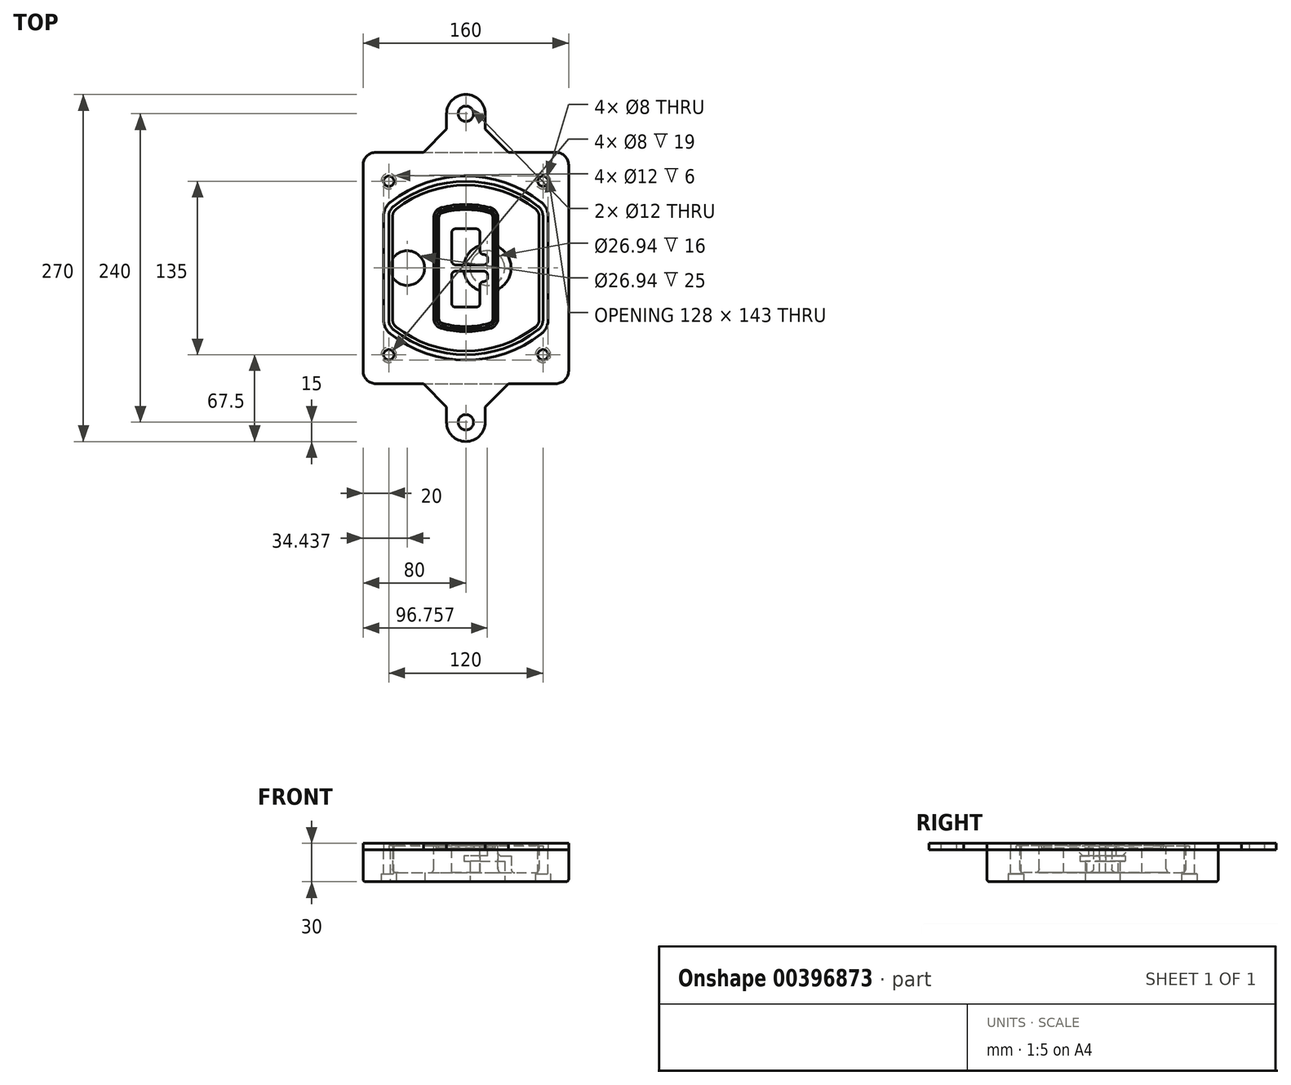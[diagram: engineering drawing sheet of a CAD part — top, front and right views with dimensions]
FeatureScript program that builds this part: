
annotation { "Feature Type Name" : "Feature", "Feature Type Description" : "" }
export const myFeature = defineFeature(function(context is Context, id is Id, definition is map)
    precondition{}
    {
        {
            var Q0;
            Q0=qCreatedBy(makeId("Top.planeOp"),FACE);
            var sketch = newSketch(context, id + "F0", { "sketchPlane" : qUnion([Q0])});
            skPoint(sketch, "E0.rect.middle", {"position": v(0, 0) * mm});
            skLineSegment(sketch, "E1.bottom", {"start": v(-70, -90) * mm, "end": v(70, -90) * mm});
            skLineSegment(sketch, "E1.top", {"start": v(-70, 90) * mm, "end": v(70, 90) * mm});
            skLineSegment(sketch, "E1.left", {"start": v(-80, -80) * mm, "end": v(-80, 80) * mm});
            skLineSegment(sketch, "E1.right", {"start": v(80, -80) * mm, "end": v(80, 80) * mm});
            skLineSegment(sketch, "E2", {"start": v(-80, 90) * mm, "end": v(80, -90) * mm, "construction": true});
            skLineSegment(sketch, "E3", {"start": v(80, 90) * mm, "end": v(-80, -90) * mm, "construction": true});
            skCircle(sketch, "E4", {"center": v(-60, 67.5) * mm, "radius": 4 * mm});
            skCircle(sketch, "E5", {"center": v(60, 67.5) * mm, "radius": 4 * mm});
            skCircle(sketch, "E6", {"center": v(60, -67.5) * mm, "radius": 4 * mm});
            skCircle(sketch, "E7", {"center": v(-60, -67.5) * mm, "radius": 4 * mm});
            skLineSegment(sketch, "E8", {"start": v(-60, 67.5) * mm, "end": v(60, 67.5) * mm, "construction": true});
            skLineSegment(sketch, "E9", {"start": v(60, 67.5) * mm, "end": v(60, -67.5) * mm, "construction": true});
            skLineSegment(sketch, "E10", {"start": v(60, -67.5) * mm, "end": v(-60, -67.5) * mm, "construction": true});
            skLineSegment(sketch, "E11", {"start": v(-60, -67.5) * mm, "end": v(-60, 67.5) * mm, "construction": true});
            skLineSegment(sketch, "E12", {"start": v(-60, 40.3) * mm, "end": v(-60, -40.3) * mm});
            skLineSegment(sketch, "E13", {"start": v(60, 40.3) * mm, "end": v(60, -40.3) * mm});
            skArc(sketch, "E14", {"start": v(56.15, 48.18) * mm, "mid": v(0, 67.5) * mm, "end": v(-56.15, 48.18) * mm});
            skArc(sketch, "E15", {"start": v(-56.15, -48.18) * mm, "mid": v(0, -67.5) * mm, "end": v(56.15, -48.18) * mm});
            skLineSegment(sketch, "E16", {"start": v(-60, 0) * mm, "end": v(60, 0) * mm, "construction": true});
            skPoint(sketch, "E17.visualSharp", {"position": v(-60, -45) * mm});
            skArc(sketch, "E17.filletArc", {"start": v(-60, -40.3) * mm, "mid": v(-58.99, -44.68) * mm, "end": v(-56.15, -48.18) * mm});
            skPoint(sketch, "E18.visualSharp", {"position": v(-60, 45) * mm});
            skArc(sketch, "E18.filletArc", {"start": v(-56.15, 48.18) * mm, "mid": v(-58.99, 44.68) * mm, "end": v(-60, 40.3) * mm});
            skPoint(sketch, "E19.visualSharp", {"position": v(60, 45) * mm});
            skArc(sketch, "E19.filletArc", {"start": v(60, 40.3) * mm, "mid": v(58.99, 44.68) * mm, "end": v(56.15, 48.18) * mm});
            skPoint(sketch, "E20.visualSharp", {"position": v(60, -45) * mm});
            skArc(sketch, "E20.filletArc", {"start": v(56.15, -48.18) * mm, "mid": v(58.99, -44.68) * mm, "end": v(60, -40.3) * mm});
            skPoint(sketch, "E21.visualSharp", {"position": v(-80, 90) * mm});
            skArc(sketch, "E21.filletArc", {"start": v(-70, 90) * mm, "mid": v(-77.07, 87.07) * mm, "end": v(-80, 80) * mm});
            skPoint(sketch, "E22.visualSharp", {"position": v(80, 90) * mm});
            skArc(sketch, "E22.filletArc", {"start": v(80, 80) * mm, "mid": v(77.07, 87.07) * mm, "end": v(70, 90) * mm});
            skPoint(sketch, "E23.visualSharp", {"position": v(80, -90) * mm});
            skArc(sketch, "E23.filletArc", {"start": v(70, -90) * mm, "mid": v(77.07, -87.07) * mm, "end": v(80, -80) * mm});
            skPoint(sketch, "E24.visualSharp", {"position": v(-80, -90) * mm});
            skArc(sketch, "E24.filletArc", {"start": v(-80, -80) * mm, "mid": v(-77.07, -87.07) * mm, "end": v(-70, -90) * mm});
            skArc(sketch, "E25.0", {"start": v(57, 40.3) * mm, "mid": v(56.3, 43.36) * mm, "end": v(54.3, 45.81) * mm});
            skLineSegment(sketch, "E25.1", {"start": v(57, 40.3) * mm, "end": v(57, -40.3) * mm});
            skArc(sketch, "E25.2", {"start": v(54.3, -45.81) * mm, "mid": v(56.3, -43.36) * mm, "end": v(57, -40.3) * mm});
            skArc(sketch, "E25.3", {"start": v(-54.3, -45.81) * mm, "mid": v(0, -64.5) * mm, "end": v(54.3, -45.81) * mm});
            skArc(sketch, "E25.4", {"start": v(-57, -40.3) * mm, "mid": v(-56.3, -43.36) * mm, "end": v(-54.3, -45.81) * mm});
            skArc(sketch, "E25.5", {"start": v(54.3, 45.81) * mm, "mid": v(0, 64.5) * mm, "end": v(-54.3, 45.81) * mm});
            skLineSegment(sketch, "E25.6", {"start": v(-57, 40.3) * mm, "end": v(-57, -40.3) * mm});
            skArc(sketch, "E25.7", {"start": v(-54.3, 45.81) * mm, "mid": v(-56.3, 43.36) * mm, "end": v(-57, 40.3) * mm});
            skArc(sketch, "E26.0", {"start": v(-58.62, 51.33) * mm, "mid": v(-62.58, 46.43) * mm, "end": v(-64, 40.3) * mm});
            skArc(sketch, "E26.1", {"start": v(58.62, 51.33) * mm, "mid": v(0, 71.5) * mm, "end": v(-58.62, 51.33) * mm});
            skArc(sketch, "E26.2", {"start": v(64, 40.3) * mm, "mid": v(62.58, 46.43) * mm, "end": v(58.62, 51.33) * mm});
            skLineSegment(sketch, "E26.3", {"start": v(64, 40.3) * mm, "end": v(64, -40.3) * mm});
            skArc(sketch, "E26.4", {"start": v(58.62, -51.33) * mm, "mid": v(62.58, -46.43) * mm, "end": v(64, -40.3) * mm});
            skLineSegment(sketch, "E26.5", {"start": v(-64, 40.3) * mm, "end": v(-64, -40.3) * mm});
            skArc(sketch, "E26.6", {"start": v(-58.62, -51.33) * mm, "mid": v(0, -71.5) * mm, "end": v(58.62, -51.33) * mm});
            skArc(sketch, "E26.7", {"start": v(-64, -40.3) * mm, "mid": v(-62.58, -46.43) * mm, "end": v(-58.62, -51.33) * mm});
            skLineSegment(sketch, "E27", {"start": v(-33, 90) * mm, "end": v(-15, 108) * mm});
            skLineSegment(sketch, "E28", {"start": v(33, 90) * mm, "end": v(15, 108) * mm});
            skLineSegment(sketch, "E29", {"start": v(15, 108) * mm, "end": v(15, 120) * mm});
            skLineSegment(sketch, "E30", {"start": v(-15, 108) * mm, "end": v(-15, 120) * mm});
            skArc(sketch, "E31", {"start": v(15, 120) * mm, "mid": v(0, 135) * mm, "end": v(-15, 120) * mm});
            skCircle(sketch, "E32", {"center": v(0, 120) * mm, "radius": 6 * mm});
            skLineSegment(sketch, "E33.MirrorCS", {"start": v(15, -108) * mm, "end": v(15, -120) * mm});
            skArc(sketch, "E34.MirrorCS", {"start": v(15, -120) * mm, "mid": v(0, -135) * mm, "end": v(-15, -120) * mm});
            skCircle(sketch, "E35.MirrorC", {"center": v(0, -120) * mm, "radius": 6 * mm});
            skLineSegment(sketch, "E36.MirrorCS", {"start": v(-15, -108) * mm, "end": v(-15, -120) * mm});
            skLineSegment(sketch, "E37.MirrorCS", {"start": v(33, -90) * mm, "end": v(15, -108) * mm});
            skLineSegment(sketch, "E38.MirrorCS", {"start": v(-33, -90) * mm, "end": v(-15, -108) * mm});
            skSolve(sketch);
        }
        {
            var Q0;
            Q0=makeQuery(id+"F0.imprint","IMPRINT",FACE,{"disambiguationData":[TD([[makeQuery(id+"F0.imprint","IMPRINT",EDGE,{"derivedFrom":sQuery(id+"F0.wireOp",EDGE,"E1.bottom")}),1.0]])]});
            var Q1;
            Q1=makeQuery(id+"F0.imprint","IMPRINT",FACE,{"disambiguationData":[TD([[makeQuery(id+"F0.imprint","IMPRINT",EDGE,{"derivedFrom":sQuery(id+"F0.wireOp",EDGE,"E12")}),1.0]])]});
            var Q2;
            Q2=makeQuery(id+"F0.imprint","IMPRINT",FACE,{"disambiguationData":[TD([[makeQuery(id+"F0.imprint","IMPRINT",EDGE,{"derivedFrom":sQuery(id+"F0.wireOp",EDGE,"E25.0")}),1.0]])]});
            var Q3;
            Q3=makeQuery(id+"F0.imprint","IMPRINT",FACE,{"disambiguationData":[TD([[makeQuery(id+"F0.imprint","IMPRINT",EDGE,{"derivedFrom":sQuery(id+"F0.wireOp",EDGE,"E12")}),-1.0]])]});
            extrude(context, id + "F1", {"entities" : qUnion([Q0, Q1, Q2, Q3]), "oppositeDirection" : true, "depth" : 25 * mm});
        }
        {
            var Q0;
            Q0=makeQuery(id+"F0.imprint","IMPRINT",FACE,{"disambiguationData":[TD([[makeQuery(id+"F0.imprint","IMPRINT",EDGE,{"derivedFrom":sQuery(id+"F0.wireOp",EDGE,"E12")}),1.0]])]});
            extrude(context, id + "F2", {"entities" : qUnion([Q0]), "operationType" : NewBodyOperationType.ADD, "depth" : 3 * mm});
        }
        {
            var Q0;
            Q0=makeQuery(id+"F0.imprint","IMPRINT",FACE,{"disambiguationData":[TD([[makeQuery(id+"F0.imprint","IMPRINT",EDGE,{"derivedFrom":sQuery(id+"F0.wireOp",EDGE,"E25.0")}),1.0]])]});
            extrude(context, id + "F3", {"entities" : qUnion([Q0]), "operationType" : NewBodyOperationType.REMOVE, "oppositeDirection" : true, "depth" : 18 * mm});
        }
        {
            var Q0;
            Q0=makeQuery(id+"F2.opExtrude","CAP_FACE",FACE,{"disambiguationData":[OSD([sQuery(id+"F0.wireOp",EDGE,"E12"),sQuery(id+"F0.wireOp",EDGE,"E13"),sQuery(id+"F0.wireOp",EDGE,"E14"),sQuery(id+"F0.wireOp",EDGE,"E15"),sQuery(id+"F0.wireOp",EDGE,"E17.filletArc"),sQuery(id+"F0.wireOp",EDGE,"E18.filletArc"),sQuery(id+"F0.wireOp",EDGE,"E19.filletArc"),sQuery(id+"F0.wireOp",EDGE,"E20.filletArc"),sQuery(id+"F0.wireOp",EDGE,"E25.0"),sQuery(id+"F0.wireOp",EDGE,"E25.1"),sQuery(id+"F0.wireOp",EDGE,"E25.2"),sQuery(id+"F0.wireOp",EDGE,"E25.3"),sQuery(id+"F0.wireOp",EDGE,"E25.4"),sQuery(id+"F0.wireOp",EDGE,"E25.5"),sQuery(id+"F0.wireOp",EDGE,"E25.6"),sQuery(id+"F0.wireOp",EDGE,"E25.7")])],"isStart":false});
            var sketch = newSketch(context, id + "F4", { "sketchPlane" : qUnion([Q0])});
            skArc(sketch, "E39.0", {"start": v(-19.08, -46.97) * mm, "mid": v(0, -49.5) * mm, "end": v(19.08, -46.97) * mm});
            skArc(sketch, "E40.0", {"start": v(19.08, 46.97) * mm, "mid": v(0, 49.5) * mm, "end": v(-19.08, 46.97) * mm});
            skLineSegment(sketch, "E41", {"start": v(-25, 39.25) * mm, "end": v(-25, -39.25) * mm});
            skLineSegment(sketch, "E42", {"start": v(25, 39.25) * mm, "end": v(25, -39.25) * mm});
            skLineSegment(sketch, "E43", {"start": v(-25, 45.1) * mm, "end": v(25, 45.1) * mm, "construction": true});
            skLineSegment(sketch, "E44", {"start": v(-25, -45.1) * mm, "end": v(25, -45.1) * mm, "construction": true});
            skPoint(sketch, "E45.visualSharp", {"position": v(-25, 45.1) * mm});
            skArc(sketch, "E45.filletArc", {"start": v(-19.08, 46.97) * mm, "mid": v(-23.35, 44.11) * mm, "end": v(-25, 39.25) * mm});
            skPoint(sketch, "E46.visualSharp", {"position": v(25, 45.1) * mm});
            skArc(sketch, "E46.filletArc", {"start": v(25, 39.25) * mm, "mid": v(23.35, 44.11) * mm, "end": v(19.08, 46.97) * mm});
            skPoint(sketch, "E47.visualSharp", {"position": v(25, -45.1) * mm});
            skArc(sketch, "E47.filletArc", {"start": v(19.08, -46.97) * mm, "mid": v(23.35, -44.11) * mm, "end": v(25, -39.25) * mm});
            skPoint(sketch, "E48.visualSharp", {"position": v(-25, -45.1) * mm});
            skArc(sketch, "E48.filletArc", {"start": v(-25, -39.25) * mm, "mid": v(-23.35, -44.11) * mm, "end": v(-19.08, -46.97) * mm});
            skArc(sketch, "E49.0", {"start": v(54.3, 45.81) * mm, "mid": v(0, 64.5) * mm, "end": v(-54.3, 45.81) * mm});
            skArc(sketch, "E49.1", {"start": v(-54.3, 45.81) * mm, "mid": v(-56.3, 43.36) * mm, "end": v(-57, 40.3) * mm});
            skLineSegment(sketch, "E49.2", {"start": v(-57, 40.3) * mm, "end": v(-57, -40.3) * mm});
            skArc(sketch, "E49.3", {"start": v(-57, -40.3) * mm, "mid": v(-56.3, -43.36) * mm, "end": v(-54.3, -45.81) * mm});
            skArc(sketch, "E49.4", {"start": v(-54.3, -45.81) * mm, "mid": v(0, -64.5) * mm, "end": v(54.3, -45.81) * mm});
            skArc(sketch, "E49.5", {"start": v(54.3, -45.81) * mm, "mid": v(56.3, -43.36) * mm, "end": v(57, -40.3) * mm});
            skLineSegment(sketch, "E49.6", {"start": v(57, 40.3) * mm, "end": v(57, -40.3) * mm});
            skArc(sketch, "E49.7", {"start": v(57, 40.3) * mm, "mid": v(56.3, 43.36) * mm, "end": v(54.3, 45.81) * mm});
            skLineSegment(sketch, "E50.0", {"start": v(23, 39.25) * mm, "end": v(23, -39.25) * mm});
            skArc(sketch, "E50.1", {"start": v(18.56, -45.04) * mm, "mid": v(21.76, -42.9) * mm, "end": v(23, -39.25) * mm});
            skArc(sketch, "E50.2", {"start": v(-18.56, -45.04) * mm, "mid": v(0, -47.5) * mm, "end": v(18.56, -45.04) * mm});
            skArc(sketch, "E50.3", {"start": v(-23, -39.25) * mm, "mid": v(-21.76, -42.9) * mm, "end": v(-18.56, -45.04) * mm});
            skLineSegment(sketch, "E50.4", {"start": v(-23, 39.25) * mm, "end": v(-23, -39.25) * mm});
            skArc(sketch, "E50.5", {"start": v(23, 39.25) * mm, "mid": v(21.76, 42.9) * mm, "end": v(18.56, 45.04) * mm});
            skArc(sketch, "E50.6", {"start": v(-18.56, 45.04) * mm, "mid": v(-21.76, 42.9) * mm, "end": v(-23, 39.25) * mm});
            skArc(sketch, "E50.7", {"start": v(18.56, 45.04) * mm, "mid": v(0, 47.5) * mm, "end": v(-18.56, 45.04) * mm});
            skArc(sketch, "E51.0", {"start": v(21, 39.25) * mm, "mid": v(20.18, 41.68) * mm, "end": v(18.04, 43.1) * mm});
            skLineSegment(sketch, "E51.1", {"start": v(21, 39.25) * mm, "end": v(21, -39.25) * mm});
            skArc(sketch, "E51.2", {"start": v(18.04, -43.1) * mm, "mid": v(20.18, -41.68) * mm, "end": v(21, -39.25) * mm});
            skArc(sketch, "E51.3", {"start": v(-18.04, -43.1) * mm, "mid": v(0, -45.5) * mm, "end": v(18.04, -43.1) * mm});
            skArc(sketch, "E51.4", {"start": v(-21, -39.25) * mm, "mid": v(-20.18, -41.68) * mm, "end": v(-18.04, -43.1) * mm});
            skArc(sketch, "E51.5", {"start": v(18.04, 43.1) * mm, "mid": v(0, 45.5) * mm, "end": v(-18.04, 43.1) * mm});
            skLineSegment(sketch, "E51.6", {"start": v(-21, 39.25) * mm, "end": v(-21, -39.25) * mm});
            skArc(sketch, "E51.7", {"start": v(-18.04, 43.1) * mm, "mid": v(-20.18, 41.68) * mm, "end": v(-21, 39.25) * mm});
            skLineSegment(sketch, "E52", {"start": v(-25, 0) * mm, "end": v(25, 0) * mm, "construction": true});
            skLineSegment(sketch, "E53", {"start": v(-11, 5.5) * mm, "end": v(-11, 27.5) * mm});
            skLineSegment(sketch, "E54", {"start": v(-8, 30.5) * mm, "end": v(8, 30.5) * mm});
            skLineSegment(sketch, "E55", {"start": v(11, 27.5) * mm, "end": v(11, 13.5) * mm});
            skLineSegment(sketch, "E56", {"start": v(14, 10.5) * mm, "end": v(14, 10.5) * mm});
            skLineSegment(sketch, "E57", {"start": v(17, 7.5) * mm, "end": v(17, 5.5) * mm});
            skLineSegment(sketch, "E58", {"start": v(14, 2.5) * mm, "end": v(-8, 2.5) * mm});
            skPoint(sketch, "E59.visualSharp", {"position": v(-11, 30.5) * mm});
            skArc(sketch, "E59.filletArc", {"start": v(-8, 30.5) * mm, "mid": v(-10.12, 29.62) * mm, "end": v(-11, 27.5) * mm});
            skPoint(sketch, "E60.visualSharp", {"position": v(11, 30.5) * mm});
            skArc(sketch, "E60.filletArc", {"start": v(11, 27.5) * mm, "mid": v(10.12, 29.62) * mm, "end": v(8, 30.5) * mm});
            skPoint(sketch, "E61.visualSharp", {"position": v(11, 10.5) * mm});
            skArc(sketch, "E61.filletArc", {"start": v(11, 13.5) * mm, "mid": v(11.88, 11.38) * mm, "end": v(14, 10.5) * mm});
            skPoint(sketch, "E62.visualSharp", {"position": v(17, 10.5) * mm});
            skArc(sketch, "E62.filletArc", {"start": v(17, 7.5) * mm, "mid": v(16.12, 9.62) * mm, "end": v(14, 10.5) * mm});
            skPoint(sketch, "E63.visualSharp", {"position": v(17, 2.5) * mm});
            skArc(sketch, "E63.filletArc", {"start": v(14, 2.5) * mm, "mid": v(16.12, 3.38) * mm, "end": v(17, 5.5) * mm});
            skPoint(sketch, "E64.visualSharp", {"position": v(-11, 2.5) * mm});
            skArc(sketch, "E64.filletArc", {"start": v(-11, 5.5) * mm, "mid": v(-10.12, 3.38) * mm, "end": v(-8, 2.5) * mm});
            skLineSegment(sketch, "E65.0.MirrorCS", {"start": v(14, -2.5) * mm, "end": v(-8, -2.5) * mm});
            skArc(sketch, "E66.0.MirrorCS", {"start": v(-11, -5.5) * mm, "mid": v(-10.12, -3.38) * mm, "end": v(-8, -2.5) * mm});
            skLineSegment(sketch, "E67.0.MirrorCS", {"start": v(-11, -5.5) * mm, "end": v(-11, -27.5) * mm});
            skArc(sketch, "E68.0.MirrorCS", {"start": v(-8, -30.5) * mm, "mid": v(-10.12, -29.62) * mm, "end": v(-11, -27.5) * mm});
            skLineSegment(sketch, "E69.0.MirrorCS", {"start": v(-8, -30.5) * mm, "end": v(8, -30.5) * mm});
            skArc(sketch, "E70.0.MirrorCS", {"start": v(11, -27.5) * mm, "mid": v(10.12, -29.62) * mm, "end": v(8, -30.5) * mm});
            skLineSegment(sketch, "E71.0.MirrorCS", {"start": v(11, -27.5) * mm, "end": v(11, -13.5) * mm});
            skArc(sketch, "E72.0.MirrorCS", {"start": v(11, -13.5) * mm, "mid": v(11.88, -11.38) * mm, "end": v(14, -10.5) * mm});
            skArc(sketch, "E73.0.MirrorCS", {"start": v(17, -7.5) * mm, "mid": v(16.12, -9.62) * mm, "end": v(14, -10.5) * mm});
            skLineSegment(sketch, "E74.0.MirrorCS", {"start": v(17, -7.5) * mm, "end": v(17, -5.5) * mm});
            skArc(sketch, "E75.0.MirrorCS", {"start": v(14, -2.5) * mm, "mid": v(16.12, -3.38) * mm, "end": v(17, -5.5) * mm});
            skSolve(sketch);
        }
        {
            var Q0;
            Q0=makeQuery(id+"F4.imprint","IMPRINT",FACE,{"disambiguationData":[TD([[makeQuery(id+"F4.imprint","IMPRINT",EDGE,{"derivedFrom":sQuery(id+"F4.wireOp",EDGE,"E39.0")}),1.0]])]});
            var Q1;
            Q1=makeQuery(id+"F4.imprint","IMPRINT",FACE,{"disambiguationData":[TD([[makeQuery(id+"F4.imprint","IMPRINT",EDGE,{"derivedFrom":sQuery(id+"F4.wireOp",EDGE,"E50.0")}),-1.0]])]});
            var Q2;
            Q2=makeQuery(id+"F4.imprint","IMPRINT",FACE,{"disambiguationData":[TD([[makeQuery(id+"F4.imprint","IMPRINT",EDGE,{"derivedFrom":sQuery(id+"F4.wireOp",EDGE,"E51.0")}),1.0]])]});
            extrude(context, id + "F5", {"entities" : qUnion([Q0, Q1, Q2]), "operationType" : NewBodyOperationType.ADD, "endBound" : BoundingType.UP_TO_NEXT, "oppositeDirection" : true, "depth" : 25 * mm});
        }
        {
            var Q0;
            Q0=makeQuery(id+"F4.imprint","IMPRINT",FACE,{"disambiguationData":[TD([[makeQuery(id+"F4.imprint","IMPRINT",EDGE,{"derivedFrom":sQuery(id+"F4.wireOp",EDGE,"E50.0")}),-1.0]])]});
            extrude(context, id + "F6", {"entities" : qUnion([Q0]), "operationType" : NewBodyOperationType.REMOVE, "oppositeDirection" : true, "depth" : 2 * mm});
        }
        {
            var Q0;
            Q0=makeQuery(id+"F1.opExtrude","CAP_FACE",FACE,{"disambiguationData":[OSD([sQuery(id+"F0.wireOp",EDGE,"E1.bottom"),sQuery(id+"F0.wireOp",EDGE,"E1.top"),sQuery(id+"F0.wireOp",EDGE,"E1.left"),sQuery(id+"F0.wireOp",EDGE,"E1.right"),sQuery(id+"F0.wireOp",EDGE,"E4"),sQuery(id+"F0.wireOp",EDGE,"E5"),sQuery(id+"F0.wireOp",EDGE,"E6"),sQuery(id+"F0.wireOp",EDGE,"E7"),sQuery(id+"F0.wireOp",EDGE,"E21.filletArc"),sQuery(id+"F0.wireOp",EDGE,"E22.filletArc"),sQuery(id+"F0.wireOp",EDGE,"E23.filletArc"),sQuery(id+"F0.wireOp",EDGE,"E24.filletArc")])],"isStart":false});
            var sketch = newSketch(context, id + "F7", { "sketchPlane" : qUnion([Q0])});
            skCircle(sketch, "E76", {"center": v(16.76, 0) * mm, "radius": 13.47 * mm});
            skCircle(sketch, "E77", {"center": v(-45.56, 0) * mm, "radius": 13.47 * mm});
            skLineSegment(sketch, "E78", {"start": v(80, 0) * mm, "end": v(-80, 0) * mm});
            skCircle(sketch, "E79", {"center": v(16.76, 0) * mm, "radius": 18.47 * mm});
            skCircle(sketch, "E80", {"center": v(60, -67.5) * mm, "radius": 6 * mm});
            skCircle(sketch, "E81", {"center": v(-60, -67.5) * mm, "radius": 6 * mm});
            skCircle(sketch, "E82", {"center": v(-60, 67.5) * mm, "radius": 6 * mm});
            skCircle(sketch, "E83", {"center": v(60, 67.5) * mm, "radius": 6 * mm});
            skSolve(sketch);
        }
        {
            var Q0;
            {var subQ1=sQuery(id+"F7.wireOp",EDGE,"E78");var subQ4=sQuery(id+"F7.wireOp",EDGE,"E76");var subQ6=makeQuery(id+"F7.imprint","INTERSECT",VERTEX,{"disambiguationData":[OD(0.0)],"derivedFrom":[subQ4,subQ1]});Q0=makeQuery(id+"F7.imprint","IMPRINT",FACE,{"disambiguationData":[TD([[makeQuery(id+"F7.imprint","IMPRINT",EDGE,{"disambiguationData":[TD([[subQ6,-1.0]])],"derivedFrom":subQ4}),-1.0]])]});}
            var Q1;
            {var subQ0=sQuery(id+"F7.wireOp",EDGE,"E78");var subQ1=sQuery(id+"F7.wireOp",EDGE,"E76");var subQ3=makeQuery(id+"F7.imprint","INTERSECT",VERTEX,{"disambiguationData":[OD(0.0)],"derivedFrom":[subQ1,subQ0]});Q1=makeQuery(id+"F7.imprint","IMPRINT",FACE,{"disambiguationData":[TD([[makeQuery(id+"F7.imprint","IMPRINT",EDGE,{"disambiguationData":[TD([[subQ3,-1.0]])],"derivedFrom":subQ1}),1.0]])]});}
            var Q2;
            {var subQ0=sQuery(id+"F7.wireOp",EDGE,"E78");var subQ1=sQuery(id+"F7.wireOp",EDGE,"E76");var subQ3=makeQuery(id+"F7.imprint","INTERSECT",VERTEX,{"disambiguationData":[OD(0.0)],"derivedFrom":[subQ1,subQ0]});Q2=makeQuery(id+"F7.imprint","IMPRINT",FACE,{"disambiguationData":[TD([[makeQuery(id+"F7.imprint","IMPRINT",EDGE,{"disambiguationData":[TD([[subQ3,1.0]])],"derivedFrom":subQ1}),1.0]])]});}
            var Q3;
            {var subQ1=sQuery(id+"F7.wireOp",EDGE,"E78");var subQ4=sQuery(id+"F7.wireOp",EDGE,"E76");var subQ6=makeQuery(id+"F7.imprint","INTERSECT",VERTEX,{"disambiguationData":[OD(0.0)],"derivedFrom":[subQ4,subQ1]});Q3=makeQuery(id+"F7.imprint","IMPRINT",FACE,{"disambiguationData":[TD([[makeQuery(id+"F7.imprint","IMPRINT",EDGE,{"disambiguationData":[TD([[subQ6,1.0]])],"derivedFrom":subQ4}),-1.0]])]});}
            extrude(context, id + "F8", {"entities" : qUnion([Q0, Q1, Q2, Q3]), "operationType" : NewBodyOperationType.ADD, "oppositeDirection" : true, "depth" : 20 * mm});
        }
        {
            var Q0;
            {var subQ0=sQuery(id+"F7.wireOp",EDGE,"E78");var subQ1=sQuery(id+"F7.wireOp",EDGE,"E76");var subQ3=makeQuery(id+"F7.imprint","INTERSECT",VERTEX,{"disambiguationData":[OD(0.0)],"derivedFrom":[subQ1,subQ0]});Q0=makeQuery(id+"F7.imprint","IMPRINT",FACE,{"disambiguationData":[TD([[makeQuery(id+"F7.imprint","IMPRINT",EDGE,{"disambiguationData":[TD([[subQ3,-1.0]])],"derivedFrom":subQ1}),1.0]])]});}
            var Q1;
            {var subQ0=sQuery(id+"F7.wireOp",EDGE,"E78");var subQ1=sQuery(id+"F7.wireOp",EDGE,"E76");var subQ3=makeQuery(id+"F7.imprint","INTERSECT",VERTEX,{"disambiguationData":[OD(0.0)],"derivedFrom":[subQ1,subQ0]});Q1=makeQuery(id+"F7.imprint","IMPRINT",FACE,{"disambiguationData":[TD([[makeQuery(id+"F7.imprint","IMPRINT",EDGE,{"disambiguationData":[TD([[subQ3,1.0]])],"derivedFrom":subQ1}),1.0]])]});}
            extrude(context, id + "F9", {"entities" : qUnion([Q0, Q1]), "operationType" : NewBodyOperationType.REMOVE, "oppositeDirection" : true, "depth" : 16 * mm});
        }
        {
            var Q0;
            {var subQ0=sQuery(id+"F7.wireOp",EDGE,"E78");var subQ1=sQuery(id+"F7.wireOp",EDGE,"E77");var subQ3=makeQuery(id+"F7.imprint","INTERSECT",VERTEX,{"disambiguationData":[OD(0.0)],"derivedFrom":[subQ1,subQ0]});Q0=makeQuery(id+"F7.imprint","IMPRINT",FACE,{"disambiguationData":[TD([[makeQuery(id+"F7.imprint","IMPRINT",EDGE,{"disambiguationData":[TD([[subQ3,-1.0]])],"derivedFrom":subQ1}),1.0]])]});}
            var Q1;
            {var subQ0=sQuery(id+"F7.wireOp",EDGE,"E78");var subQ1=sQuery(id+"F7.wireOp",EDGE,"E77");var subQ3=makeQuery(id+"F7.imprint","INTERSECT",VERTEX,{"disambiguationData":[OD(0.0)],"derivedFrom":[subQ1,subQ0]});Q1=makeQuery(id+"F7.imprint","IMPRINT",FACE,{"disambiguationData":[TD([[makeQuery(id+"F7.imprint","IMPRINT",EDGE,{"disambiguationData":[TD([[subQ3,1.0]])],"derivedFrom":subQ1}),1.0]])]});}
            extrude(context, id + "F10", {"entities" : qUnion([Q0, Q1]), "operationType" : NewBodyOperationType.REMOVE, "oppositeDirection" : true, "depth" : 25 * mm});
        }
        {
            var Q0;
            Q0=makeQuery(id+"F7.imprint","IMPRINT",FACE,{"disambiguationData":[TD([[makeQuery(id+"F7.imprint","IMPRINT",EDGE,{"derivedFrom":sQuery(id+"F7.wireOp",EDGE,"E80")}),1.0]])]});
            var Q1;
            Q1=makeQuery(id+"F7.imprint","IMPRINT",FACE,{"disambiguationData":[TD([[makeQuery(id+"F7.imprint","IMPRINT",EDGE,{"derivedFrom":makeQuery(id+"F1.opExtrude","CAP_EDGE",EDGE,{"disambiguationData":[OSD([sQuery(id+"F0.wireOp",EDGE,"E5")])],"isStart":false})}),-1.0]])]});
            var Q2;
            Q2=makeQuery(id+"F7.imprint","IMPRINT",FACE,{"disambiguationData":[TD([[makeQuery(id+"F7.imprint","IMPRINT",EDGE,{"derivedFrom":sQuery(id+"F7.wireOp",EDGE,"E81")}),1.0]])]});
            var Q3;
            Q3=makeQuery(id+"F7.imprint","IMPRINT",FACE,{"disambiguationData":[TD([[makeQuery(id+"F7.imprint","IMPRINT",EDGE,{"derivedFrom":makeQuery(id+"F1.opExtrude","CAP_EDGE",EDGE,{"disambiguationData":[OSD([sQuery(id+"F0.wireOp",EDGE,"E4")])],"isStart":false})}),-1.0]])]});
            var Q4;
            Q4=makeQuery(id+"F7.imprint","IMPRINT",FACE,{"disambiguationData":[TD([[makeQuery(id+"F7.imprint","IMPRINT",EDGE,{"derivedFrom":sQuery(id+"F7.wireOp",EDGE,"E82")}),1.0]])]});
            var Q5;
            Q5=makeQuery(id+"F7.imprint","IMPRINT",FACE,{"disambiguationData":[TD([[makeQuery(id+"F7.imprint","IMPRINT",EDGE,{"derivedFrom":makeQuery(id+"F1.opExtrude","CAP_EDGE",EDGE,{"disambiguationData":[OSD([sQuery(id+"F0.wireOp",EDGE,"E7")])],"isStart":false})}),-1.0]])]});
            var Q6;
            Q6=makeQuery(id+"F7.imprint","IMPRINT",FACE,{"disambiguationData":[TD([[makeQuery(id+"F7.imprint","IMPRINT",EDGE,{"derivedFrom":sQuery(id+"F7.wireOp",EDGE,"E83")}),1.0]])]});
            var Q7;
            Q7=makeQuery(id+"F7.imprint","IMPRINT",FACE,{"disambiguationData":[TD([[makeQuery(id+"F7.imprint","IMPRINT",EDGE,{"derivedFrom":makeQuery(id+"F1.opExtrude","CAP_EDGE",EDGE,{"disambiguationData":[OSD([sQuery(id+"F0.wireOp",EDGE,"E6")])],"isStart":false})}),-1.0]])]});
            extrude(context, id + "F11", {"entities" : qUnion([Q0, Q1, Q2, Q3, Q4, Q5, Q6, Q7]), "operationType" : NewBodyOperationType.REMOVE, "oppositeDirection" : true, "depth" : 6 * mm});
        }
        {
            var Q0;
            Q0=makeQuery(id+"F9.boolean.opBoolean","COPY",FACE,{"derivedFrom":makeQuery(id+"F9.opExtrude","CAP_FACE",FACE,{"disambiguationData":[OSD([sQuery(id+"F7.wireOp",EDGE,"E76")])],"isStart":false})});
            var sketch = newSketch(context, id + "F12", { "sketchPlane" : qUnion([Q0])});
            skArc(sketch, "E84.0", {"start": v(11, 17.55) * mm, "mid": v(2.57, 11.82) * mm, "end": v(-1.54, 2.5) * mm});
            skArc(sketch, "E84.1", {"start": v(-1.54, -2.5) * mm, "mid": v(2.57, -11.82) * mm, "end": v(11, -17.55) * mm});
            skLineSegment(sketch, "E85", {"start": v(-1.54, -2.5) * mm, "end": v(14, -2.5) * mm});
            skLineSegment(sketch, "E86.0", {"start": v(14, 2.5) * mm, "end": v(-1.54, 2.5) * mm});
            skArc(sketch, "E86.1", {"start": v(14, 2.5) * mm, "mid": v(16.12, 3.38) * mm, "end": v(17, 5.5) * mm});
            skLineSegment(sketch, "E86.2", {"start": v(17, 7.5) * mm, "end": v(17, 5.5) * mm});
            skArc(sketch, "E86.3", {"start": v(17, 7.5) * mm, "mid": v(16.12, 9.62) * mm, "end": v(14, 10.5) * mm});
            skArc(sketch, "E86.4", {"start": v(11, 13.5) * mm, "mid": v(11.88, 11.38) * mm, "end": v(14, 10.5) * mm});
            skLineSegment(sketch, "E86.5", {"start": v(11, 17.55) * mm, "end": v(11, 13.5) * mm});
            skLineSegment(sketch, "E86.7", {"start": v(14, -2.5) * mm, "end": v(-1.54, -2.5) * mm});
            skArc(sketch, "E86.8", {"start": v(14, -2.5) * mm, "mid": v(16.12, -3.38) * mm, "end": v(17, -5.5) * mm});
            skLineSegment(sketch, "E86.9", {"start": v(17, -7.5) * mm, "end": v(17, -5.5) * mm});
            skArc(sketch, "E86.10", {"start": v(17, -7.5) * mm, "mid": v(16.12, -9.62) * mm, "end": v(14, -10.5) * mm});
            skArc(sketch, "E86.11", {"start": v(11, -13.5) * mm, "mid": v(11.88, -11.38) * mm, "end": v(14, -10.5) * mm});
            skLineSegment(sketch, "E86.12", {"start": v(11, -17.55) * mm, "end": v(11, -13.5) * mm});
            skPoint(sketch, "E87.orphan", {"position": v(11, -27.5) * mm});
            skPoint(sketch, "E88.orphan", {"position": v(-8, -2.5) * mm});
            skPoint(sketch, "E89.orphan", {"position": v(-8, 2.5) * mm});
            skPoint(sketch, "E90.orphan", {"position": v(11, 27.5) * mm});
            skSolve(sketch);
        }
        {
            var Q0;
            {var subQ7=sQuery(id+"F12.wireOp",EDGE,"E84.0");var subQ14=sQuery(id+"F12.wireOp",EDGE,"E84.1");var subQ16=sQuery(id+"F12.wireOp",EDGE,"E86.1");var subQ18=sQuery(id+"F12.wireOp",EDGE,"E86.8");Q0=qUnion([makeQuery(id+"F12.imprint","IMPRINT",FACE,{"disambiguationData":[TD([[makeQuery(id+"F12.imprint","IMPRINT",EDGE,{"derivedFrom":subQ7}),1.0]])]}),makeQuery(id+"F12.imprint","IMPRINT",FACE,{"disambiguationData":[TD([[makeQuery(id+"F12.imprint","IMPRINT",EDGE,{"derivedFrom":subQ14}),1.0]])]}),makeQuery(id+"F12.imprint","IMPRINT",FACE,{"disambiguationData":[TD([[makeQuery(id+"F12.imprint","IMPRINT",EDGE,{"derivedFrom":subQ16}),1.0]])]}),makeQuery(id+"F12.imprint","IMPRINT",FACE,{"disambiguationData":[TD([[makeQuery(id+"F12.imprint","IMPRINT",EDGE,{"derivedFrom":subQ18}),-1.0]])]})]);}
            var Q1;
            Q1=makeQuery(id+"F5.boolean.opBoolean","SPLIT",FACE,{"disambiguationData":[TD([makeQuery(id+"F5.opExtrude","SWEPT_FACE",FACE,{"disambiguationData":[OSD([sQuery(id+"F4.wireOp",EDGE,"E53")])]})])],"derivedFrom":makeQuery(id+"F3.boolean.opBoolean","COPY",FACE,{"derivedFrom":makeQuery(id+"F3.opExtrude","CAP_FACE",FACE,{"disambiguationData":[OSD([sQuery(id+"F0.wireOp",EDGE,"E25.0"),sQuery(id+"F0.wireOp",EDGE,"E25.1"),sQuery(id+"F0.wireOp",EDGE,"E25.2"),sQuery(id+"F0.wireOp",EDGE,"E25.3"),sQuery(id+"F0.wireOp",EDGE,"E25.4"),sQuery(id+"F0.wireOp",EDGE,"E25.5"),sQuery(id+"F0.wireOp",EDGE,"E25.6"),sQuery(id+"F0.wireOp",EDGE,"E25.7")])],"isStart":false})})});
            extrude(context, id + "F13", {"entities" : qUnion([Q0]), "operationType" : NewBodyOperationType.REMOVE, "endBound" : BoundingType.UP_TO_SURFACE, "endBoundEntityFace" : qUnion([Q1]), "depth" : 25 * mm});
        }
        {
            var Q0;
            Q0=makeQuery(id+"F3.boolean.opBoolean","COPY",EDGE,{"derivedFrom":makeQuery(id+"F3.opExtrude","CAP_EDGE",EDGE,{"disambiguationData":[OSD([sQuery(id+"F0.wireOp",EDGE,"E25.6")])],"isStart":false})});
            var Q1;
            Q1=makeQuery(id+"F8.boolean.opBoolean","INTERSECT",EDGE,{"derivedFrom":[makeQuery(id+"F5.opExtrude","SWEPT_FACE",FACE,{"disambiguationData":[OSD([sQuery(id+"F4.wireOp",EDGE,"E42")])]}),makeQuery(id+"F8.opExtrude","CAP_FACE",FACE,{"disambiguationData":[OSD([sQuery(id+"F7.wireOp",EDGE,"E79")])],"isStart":false})]});
            var Q2;
            Q2=makeQuery(id+"F8.boolean.opBoolean","INTERSECT",EDGE,{"disambiguationData":[OD(1.0)],"derivedFrom":[makeQuery(id+"F5.opExtrude","SWEPT_FACE",FACE,{"disambiguationData":[OSD([sQuery(id+"F4.wireOp",EDGE,"E42")])]}),makeQuery(id+"F8.opExtrude","SWEPT_FACE",FACE,{"disambiguationData":[OSD([sQuery(id+"F7.wireOp",EDGE,"E79")])]})]});
            var Q3;
            {var subQ0=sQuery(id+"F4.wireOp",EDGE,"E42");Q3=makeQuery(id+"F8.boolean.opBoolean","SPLIT",EDGE,{"disambiguationData":[TD([makeQuery(id+"F5.opExtrude","SWEPT_FACE",FACE,{"disambiguationData":[OSD([sQuery(id+"F4.wireOp",EDGE,"E47.filletArc")])]})])],"derivedFrom":makeQuery(id+"F5.opExtrude","CAP_EDGE",EDGE,{"disambiguationData":[OSD([subQ0])],"isStart":false})});}
            var Q4;
            {var subQ0=sQuery(id+"F0.wireOp",EDGE,"E25.7");var subQ1=sQuery(id+"F0.wireOp",EDGE,"E25.1");var subQ2=sQuery(id+"F0.wireOp",EDGE,"E25.6");var subQ3=sQuery(id+"F0.wireOp",EDGE,"E25.5");var subQ4=sQuery(id+"F0.wireOp",EDGE,"E25.4");var subQ5=sQuery(id+"F0.wireOp",EDGE,"E25.0");var subQ6=sQuery(id+"F0.wireOp",EDGE,"E25.2");var subQ7=sQuery(id+"F0.wireOp",EDGE,"E25.3");Q4=makeQuery(id+"F8.boolean.opBoolean","INTERSECT",EDGE,{"derivedFrom":[makeQuery(id+"F5.boolean.opBoolean","SPLIT",FACE,{"disambiguationData":[TD([makeQuery(id+"F2.opExtrude","SWEPT_FACE",FACE,{"disambiguationData":[OSD([subQ5])]})])],"derivedFrom":makeQuery(id+"F3.boolean.opBoolean","COPY",FACE,{"derivedFrom":makeQuery(id+"F3.opExtrude","CAP_FACE",FACE,{"disambiguationData":[OSD([subQ5,subQ1,subQ6,subQ7,subQ4,subQ3,subQ2,subQ0])],"isStart":false})})}),makeQuery(id+"F8.opExtrude","SWEPT_FACE",FACE,{"disambiguationData":[OSD([sQuery(id+"F7.wireOp",EDGE,"E79")])]})]});}
            var Q5;
            Q5=makeQuery(id+"F8.boolean.opBoolean","INTERSECT",EDGE,{"disambiguationData":[OD(0.0)],"derivedFrom":[makeQuery(id+"F5.opExtrude","SWEPT_FACE",FACE,{"disambiguationData":[OSD([sQuery(id+"F4.wireOp",EDGE,"E42")])]}),makeQuery(id+"F8.opExtrude","SWEPT_FACE",FACE,{"disambiguationData":[OSD([sQuery(id+"F7.wireOp",EDGE,"E79")])]})]});
            fillet(context, id + "F14", {"entities" : qUnion([Q0, Q1, Q2, Q3, Q4, Q5]), "radius" : 3 * mm, "tangentPropagation" : true, "allowEdgeOverflow" : false});
        }
        {
            var Q0;
            Q0=makeQuery(id+"F1.opExtrude","CAP_EDGE",EDGE,{"disambiguationData":[OSD([sQuery(id+"F0.wireOp",EDGE,"E1.bottom")])],"isStart":false});
            fillet(context, id + "F15", {"entities" : qUnion([Q0]), "radius" : 2 * mm, "tangentPropagation" : true, "allowEdgeOverflow" : false});
        }
        {
            var Q0;
            Q0=qSketchRegion(id+"F0",true);
            extrude(context, id + "F16", {"entities" : qUnion([Q0]), "depth" : 5 * mm});
        }
    });
